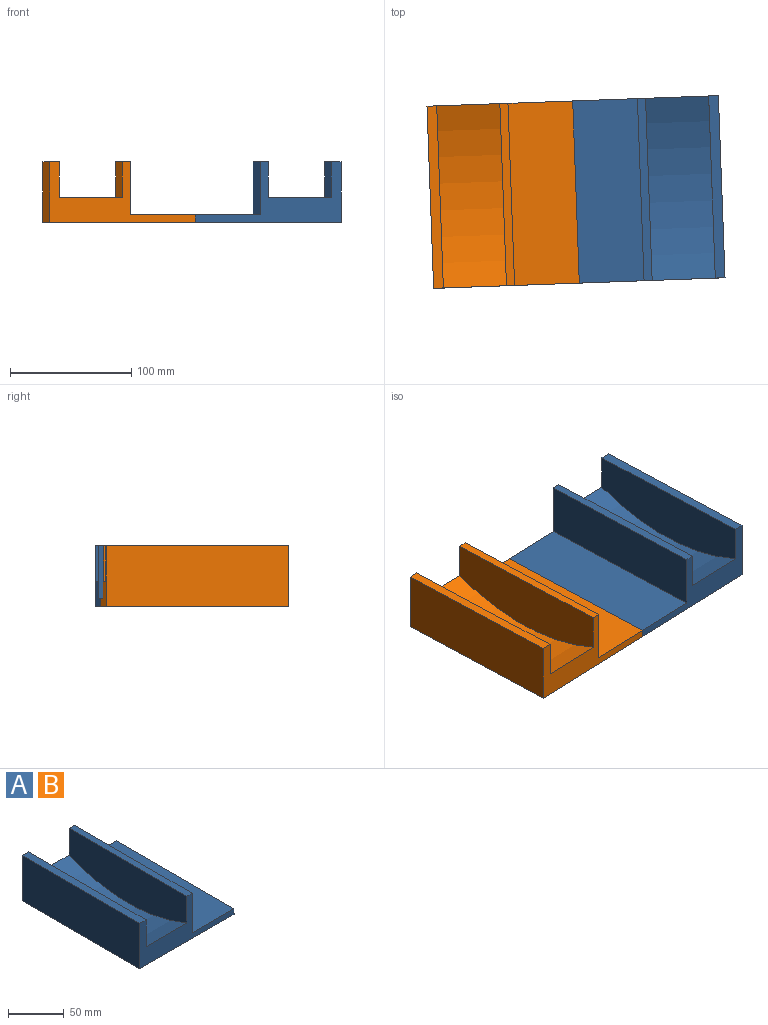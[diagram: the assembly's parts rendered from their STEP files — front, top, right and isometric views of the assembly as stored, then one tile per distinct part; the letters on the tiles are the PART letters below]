
ASSEMBLY  parts=2 mates=1
PART A: 12 faces, bbox 120x150x50 mm
  f0: plane 120x50mm, normal (0,-1,0), area 2130.4mm2, adj f1,f3,f4,f5,f6,f7,f8,f9
  f1: plane 150x6.26mm, normal (1,0,0), area 939.4mm2, adj f0,f2,f4,f11
  f2: plane 120x50mm, normal (0,1,0), area 2130.4mm2, adj f1,f3,f4,f5,f6,f7,f8,f9
  f3: plane 150x6.68mm, normal (0,0,1), area 1002.7mm2, adj f0,f2,f9,f10
  f4: plane 150x120mm, normal (0,0,-1), area 18000mm2, adj f0,f1,f2,f6
  f5: plane 150x8mm, normal (0,0,1), area 1200mm2, adj f0,f2,f6,f8
  f6: plane 150x50mm, normal (-1,0,0), area 7500mm2, adj f0,f2,f4,f5
  f7: cylinder r=190mm len=150mm, axis (1,0,0), area 8018.2mm2, adj f0,f2,f8,f9
  f8: plane 150x45mm, normal (1,0,0), area 5991.5mm2, adj f0,f2,f5,f7
  f9: plane 150x45mm, normal (-1,0,0), area 5991.5mm2, adj f0,f2,f3,f7
  f10: plane 150x43.74mm, normal (1,0,0), area 6560.6mm2, adj f0,f2,f3,f11
  f11: plane 150x53.32mm, normal (0,0,1), area 7997.3mm2, adj f0,f1,f2,f10
PART B: same geometry as A
PLACE A rot(axis=(0,0,-1),177.9deg) t=(-55.76,-18.14,-10.6)mm
PLACE B rot(axis=(0,0,1),2.1deg) t=(-55.76,-18.14,-10.6)mm
MATE parallel B.f1 <-> A.f1  axis (1,0.04,0) through (-55.76,-18.14,-32.47)mm
